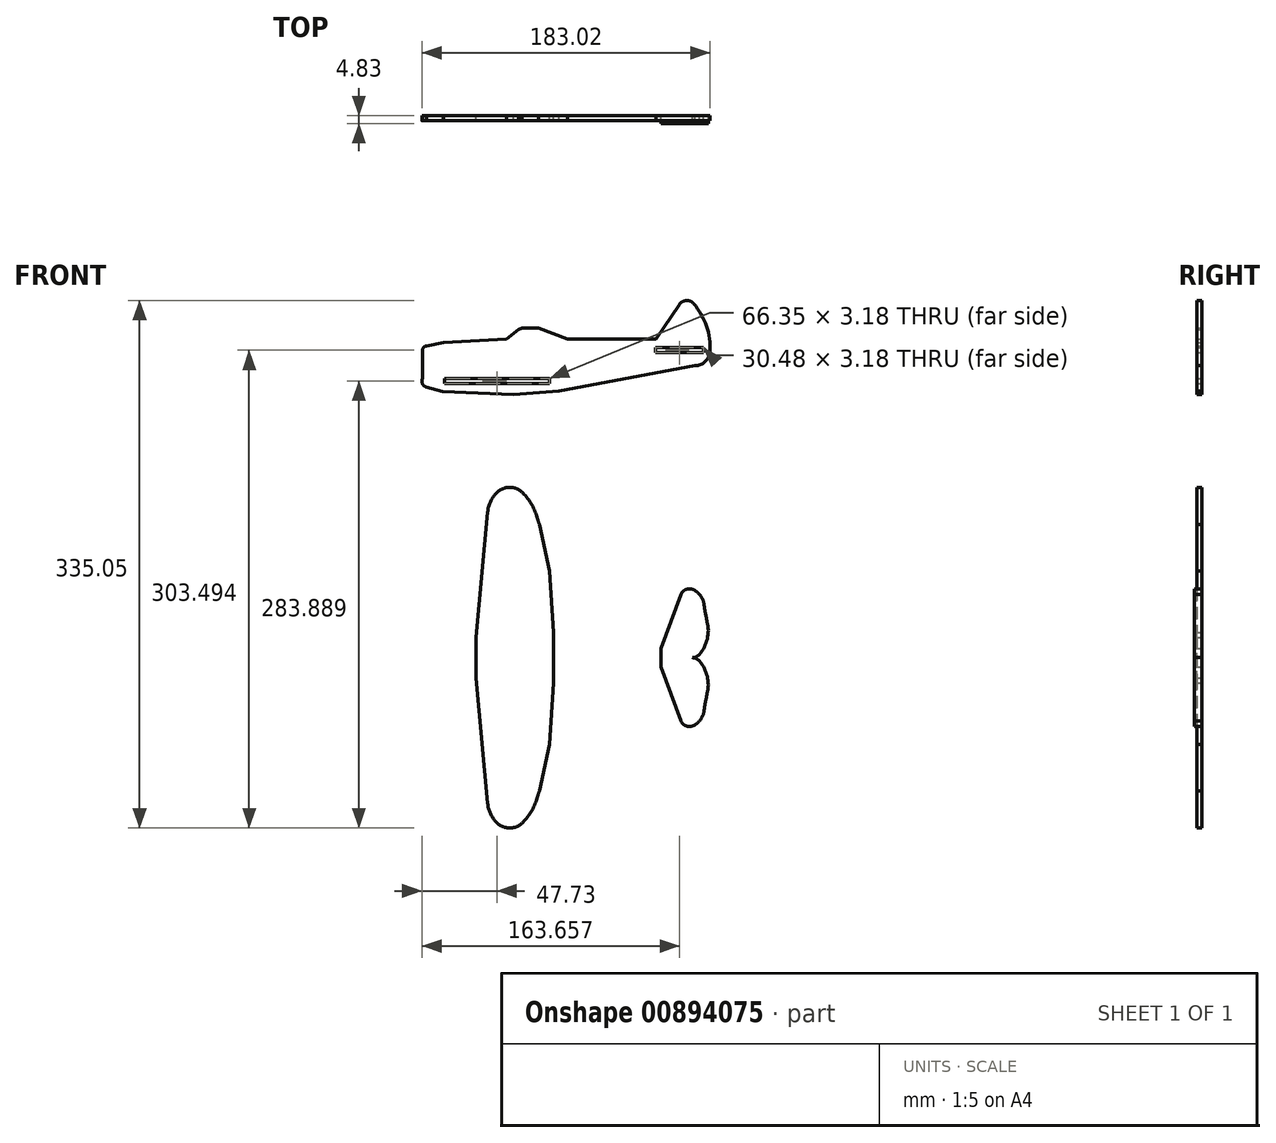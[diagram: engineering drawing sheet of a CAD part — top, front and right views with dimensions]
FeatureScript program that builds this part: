
annotation { "Feature Type Name" : "Feature", "Feature Type Description" : "" }
export const myFeature = defineFeature(function(context is Context, id is Id, definition is map)
    precondition{}
    {
        {
            var Q0;
            Q0=qCreatedBy(makeId("Front.planeOp"),FACE);
            var sketch = newSketch(context, id + "F0", { "sketchPlane" : qUnion([Q0])});
            skSolve(sketch);
        }
        {
            var Q0;
            Q0=qCreatedBy(makeId("Front.planeOp"),FACE);
            var sketch = newSketch(context, id + "F1", { "sketchPlane" : qUnion([Q0])});
            skLineSegment(sketch, "E0", {"start": v(-214.81, 114.42) * mm, "end": v(-29.22, 114.42) * mm, "construction": true});
            skLineSegment(sketch, "E1", {"start": v(-180, 114.42) * mm, "end": v(-180, 127.23) * mm, "construction": true});
            skLineSegment(sketch, "E2", {"start": v(-180, 127.23) * mm, "end": v(-172.61, 206.88) * mm});
            skArc(sketch, "E3", {"start": v(-172.61, 206.88) * mm, "mid": v(-170.85, 213.46) * mm, "end": v(-166.99, 219.08) * mm});
            skArc(sketch, "E4", {"start": v(-166.99, 219.08) * mm, "mid": v(-158.64, 222.6) * mm, "end": v(-150.3, 219.08) * mm});
            skArc(sketch, "E5", {"start": v(-150.3, 219.08) * mm, "mid": v(-144.52, 211.4) * mm, "end": v(-140.84, 202.54) * mm});
            skArc(sketch, "E6", {"start": v(-140.84, 202.54) * mm, "mid": v(-140.34, 200.83) * mm, "end": v(-139.8, 199.12) * mm});
            skLineSegment(sketch, "E7", {"start": v(-139.8, 199.12) * mm, "end": v(-133.44, 169.53) * mm});
            skLineSegment(sketch, "E8", {"start": v(-133.44, 169.53) * mm, "end": v(-130.81, 130.44) * mm});
            skLineSegment(sketch, "E9", {"start": v(-130.81, 130.44) * mm, "end": v(-130.81, 114.42) * mm});
            skLineSegment(sketch, "E10", {"start": v(-180, 114.42) * mm, "end": v(-180, 127.23) * mm});
            skLineSegment(sketch, "E11", {"start": v(-62.56, 114.42) * mm, "end": v(-62.56, 120.3) * mm});
            skLineSegment(sketch, "E12", {"start": v(-62.56, 120.3) * mm, "end": v(-49.89, 154.49) * mm});
            skArc(sketch, "E13", {"start": v(-49.89, 154.49) * mm, "mid": v(-48.63, 156.46) * mm, "end": v(-46.68, 157.74) * mm});
            skArc(sketch, "E14", {"start": v(-46.68, 157.74) * mm, "mid": v(-44.45, 158.15) * mm, "end": v(-42.23, 157.74) * mm});
            skArc(sketch, "E15", {"start": v(-42.23, 157.74) * mm, "mid": v(-39.9, 156.42) * mm, "end": v(-38.08, 154.49) * mm});
            skArc(sketch, "E16", {"start": v(-38.08, 154.49) * mm, "mid": v(-36.15, 151.58) * mm, "end": v(-35.18, 148.24) * mm});
            skArc(sketch, "E17", {"start": v(-35.18, 148.24) * mm, "mid": v(-34.3, 142.72) * mm, "end": v(-33.15, 137.26) * mm});
            skArc(sketch, "E18", {"start": v(-33.15, 137.26) * mm, "mid": v(-33.14, 126.34) * mm, "end": v(-38.08, 116.6) * mm});
            skArc(sketch, "E19", {"start": v(-38.08, 116.6) * mm, "mid": v(-40.03, 115.06) * mm, "end": v(-42.43, 114.42) * mm});
            skLineSegment(sketch, "E20", {"start": v(-213.84, 291.87) * mm, "end": v(-213.84, 309.93) * mm});
            skArc(sketch, "E21", {"start": v(-213.84, 309.93) * mm, "mid": v(-213.17, 311.66) * mm, "end": v(-211.52, 312.49) * mm});
            skLineSegment(sketch, "E22", {"start": v(-211.52, 312.49) * mm, "end": v(-200.55, 314.65) * mm});
            skLineSegment(sketch, "E23", {"start": v(-200.55, 314.65) * mm, "end": v(-160.75, 316.67) * mm});
            skLineSegment(sketch, "E24", {"start": v(-160.75, 316.67) * mm, "end": v(-152.96, 322.87) * mm});
            skLineSegment(sketch, "E25", {"start": v(-152.96, 322.87) * mm, "end": v(-150.65, 323.8) * mm});
            skLineSegment(sketch, "E26", {"start": v(-150.65, 323.8) * mm, "end": v(-140.2, 323.8) * mm});
            skLineSegment(sketch, "E27", {"start": v(-140.2, 323.8) * mm, "end": v(-121.96, 316.67) * mm});
            skLineSegment(sketch, "E28", {"start": v(-65.82, 316.67) * mm, "end": v(-50.84, 338.76) * mm});
            skArc(sketch, "E29", {"start": v(-50.84, 338.76) * mm, "mid": v(-46.41, 341.28) * mm, "end": v(-41.72, 339.29) * mm});
            skArc(sketch, "E30", {"start": v(-41.72, 339.29) * mm, "mid": v(-33.62, 325.05) * mm, "end": v(-31.44, 308.8) * mm});
            skArc(sketch, "E31", {"start": v(-31.44, 308.8) * mm, "mid": v(-34.41, 302.47) * mm, "end": v(-40.94, 299.95) * mm});
            skLineSegment(sketch, "E32", {"start": v(-40.94, 299.95) * mm, "end": v(-127.43, 283.8) * mm});
            skLineSegment(sketch, "E33", {"start": v(-127.43, 283.8) * mm, "end": v(-156.09, 281.71) * mm});
            skLineSegment(sketch, "E34", {"start": v(-156.09, 281.71) * mm, "end": v(-201.28, 283.4) * mm});
            skLineSegment(sketch, "E35", {"start": v(-201.28, 283.4) * mm, "end": v(-211.7, 286.4) * mm});
            skArc(sketch, "E36", {"start": v(-211.7, 286.4) * mm, "mid": v(-214.12, 288.6) * mm, "end": v(-213.84, 291.87) * mm});
            skArc(sketch, "E37.MirrorCS", {"start": v(-140.84, 26.3) * mm, "mid": v(-140.34, 28.02) * mm, "end": v(-139.8, 29.73) * mm});
            skLineSegment(sketch, "E38.MirrorCS", {"start": v(-180, 114.42) * mm, "end": v(-180, 101.62) * mm, "construction": true});
            skLineSegment(sketch, "E39.MirrorCS", {"start": v(-139.8, 29.73) * mm, "end": v(-133.44, 59.32) * mm});
            skArc(sketch, "E40.MirrorCS", {"start": v(-166.99, 9.77) * mm, "mid": v(-158.64, 6.24) * mm, "end": v(-150.3, 9.77) * mm});
            skArc(sketch, "E41.MirrorCS", {"start": v(-172.61, 21.97) * mm, "mid": v(-170.85, 15.39) * mm, "end": v(-166.99, 9.77) * mm});
            skLineSegment(sketch, "E42.MirrorCS", {"start": v(-133.44, 59.32) * mm, "end": v(-130.81, 98.4) * mm});
            skLineSegment(sketch, "E43.MirrorCS", {"start": v(-180, 114.42) * mm, "end": v(-180, 101.62) * mm});
            skLineSegment(sketch, "E44.MirrorCS", {"start": v(-180, 101.62) * mm, "end": v(-172.61, 21.97) * mm});
            skArc(sketch, "E45.MirrorCS", {"start": v(-150.3, 9.77) * mm, "mid": v(-144.52, 17.44) * mm, "end": v(-140.84, 26.3) * mm});
            skLineSegment(sketch, "E46.MirrorCS", {"start": v(-130.81, 98.4) * mm, "end": v(-130.81, 114.42) * mm});
            skArc(sketch, "E47.MirrorCS", {"start": v(-42.23, 71.11) * mm, "mid": v(-39.9, 72.43) * mm, "end": v(-38.08, 74.36) * mm});
            skArc(sketch, "E48.MirrorCS", {"start": v(-46.68, 71.11) * mm, "mid": v(-44.45, 70.7) * mm, "end": v(-42.23, 71.11) * mm});
            skArc(sketch, "E49.MirrorCS", {"start": v(-49.89, 74.36) * mm, "mid": v(-48.63, 72.4) * mm, "end": v(-46.68, 71.11) * mm});
            skArc(sketch, "E50.MirrorCS", {"start": v(-38.08, 112.26) * mm, "mid": v(-40.03, 113.8) * mm, "end": v(-42.43, 114.42) * mm});
            skLineSegment(sketch, "E51.MirrorCS", {"start": v(-62.56, 114.42) * mm, "end": v(-62.56, 108.55) * mm});
            skLineSegment(sketch, "E52.MirrorCS", {"start": v(-62.56, 108.55) * mm, "end": v(-49.89, 74.36) * mm});
            skArc(sketch, "E53.MirrorCS", {"start": v(-35.18, 80.61) * mm, "mid": v(-34.3, 86.13) * mm, "end": v(-33.15, 91.59) * mm});
            skArc(sketch, "E54.MirrorCS", {"start": v(-33.15, 91.59) * mm, "mid": v(-33.14, 102.51) * mm, "end": v(-38.08, 112.26) * mm});
            skArc(sketch, "E55.MirrorCS", {"start": v(-38.08, 74.36) * mm, "mid": v(-36.15, 77.27) * mm, "end": v(-35.18, 80.61) * mm});
            skLineSegment(sketch, "E56", {"start": v(-121.96, 316.67) * mm, "end": v(-65.82, 316.67) * mm});
            skSolve(sketch);
        }
        {
            var Q0;
            Q0=makeQuery(id+"F1.imprint","IMPRINT",FACE,{"disambiguationData":[TD([[makeQuery(id+"F1.imprint","IMPRINT",EDGE,{"derivedFrom":sQuery(id+"F1.wireOp",EDGE,"E2")}),-1.0]])]});
            var Q1;
            Q1=makeQuery(id+"F1.imprint","IMPRINT",FACE,{"disambiguationData":[TD([[makeQuery(id+"F1.imprint","IMPRINT",EDGE,{"derivedFrom":sQuery(id+"F1.wireOp",EDGE,"E20")}),-1.0]])]});
            var Q2;
            Q2=makeQuery(id+"F1.imprint","IMPRINT",FACE,{"disambiguationData":[TD([[makeQuery(id+"F1.imprint","IMPRINT",EDGE,{"derivedFrom":sQuery(id+"F1.wireOp",EDGE,"E11")}),-1.0]])]});
            extrude(context, id + "F2", {"entities" : qUnion([Q0, Q1, Q2]), "depth" : 3.17 * mm, "offsetDistance" : 25.4 * mm});
        }
        {
            var Q0;
            Q0=makeQuery(id+"F2.opExtrude","CAP_FACE",FACE,{"disambiguationData":[OSD([sQuery(id+"F1.wireOp",EDGE,"E20"),sQuery(id+"F1.wireOp",EDGE,"E21"),sQuery(id+"F1.wireOp",EDGE,"E22"),sQuery(id+"F1.wireOp",EDGE,"E23"),sQuery(id+"F1.wireOp",EDGE,"E24"),sQuery(id+"F1.wireOp",EDGE,"E25"),sQuery(id+"F1.wireOp",EDGE,"E26"),sQuery(id+"F1.wireOp",EDGE,"E27"),sQuery(id+"F1.wireOp",EDGE,"E28"),sQuery(id+"F1.wireOp",EDGE,"E29"),sQuery(id+"F1.wireOp",EDGE,"E30"),sQuery(id+"F1.wireOp",EDGE,"E31"),sQuery(id+"F1.wireOp",EDGE,"E32"),sQuery(id+"F1.wireOp",EDGE,"E33"),sQuery(id+"F1.wireOp",EDGE,"E34"),sQuery(id+"F1.wireOp",EDGE,"E35"),sQuery(id+"F1.wireOp",EDGE,"E36"),sQuery(id+"F1.wireOp",EDGE,"E56")])],"isStart":false});
            extrude(context, id + "F3", {"entities" : qUnion([Q0]), "operationType" : NewBodyOperationType.ADD, "depth" : 1 / 203.2 * mm, "offsetDistance" : 25.4 * mm});
        }
        {
            var Q0;
            Q0=qCreatedBy(makeId("Front.planeOp"),FACE);
            var sketch = newSketch(context, id + "F4", { "sketchPlane" : qUnion([Q0])});
            skLineSegment(sketch, "E57.bottom", {"start": v(-199.83, 291.72) * mm, "end": v(-133.47, 291.72) * mm});
            skLineSegment(sketch, "E57.top", {"start": v(-199.83, 288.54) * mm, "end": v(-133.47, 288.54) * mm});
            skLineSegment(sketch, "E57.left", {"start": v(-199.83, 291.72) * mm, "end": v(-199.83, 288.54) * mm});
            skLineSegment(sketch, "E57.right", {"start": v(-133.47, 291.72) * mm, "end": v(-133.47, 288.54) * mm});
            skLineSegment(sketch, "E58.bottom", {"start": v(-65.96, 311.32) * mm, "end": v(-35.48, 311.32) * mm});
            skLineSegment(sketch, "E58.top", {"start": v(-65.96, 308.15) * mm, "end": v(-35.48, 308.15) * mm});
            skLineSegment(sketch, "E58.left", {"start": v(-65.96, 311.32) * mm, "end": v(-65.96, 308.15) * mm});
            skLineSegment(sketch, "E58.right", {"start": v(-35.48, 311.32) * mm, "end": v(-35.48, 308.15) * mm});
            skLineSegment(sketch, "E59", {"start": v(-180.49, 127.2) * mm, "end": v(-180.49, 99.94) * mm, "construction": true});
            skLineSegment(sketch, "E60", {"start": v(-62.89, 115.5) * mm, "end": v(-35.32, 115.5) * mm, "construction": true});
            skSolve(sketch);
        }
        {
            var Q0;
            Q0 = qSketchRegion(id + "F4", true);
            extrude(context, id + "F5", {"entities" : qUnion([Q0]), "operationType" : NewBodyOperationType.REMOVE, "endBound" : BoundingType.THROUGH_ALL, "depth" : 25.4 * mm, "offsetDistance" : 25.4 * mm});
        }
        {
            var Q0;
            Q0 = qSketchRegion(id + "F0", true);
            var Q1;
            Q1=makeQuery(id+"F2.opExtrude","CAP_FACE",FACE,{"disambiguationData":[OSD([sQuery(id+"F1.wireOp",EDGE,"E11"),sQuery(id+"F1.wireOp",EDGE,"E12"),sQuery(id+"F1.wireOp",EDGE,"E13"),sQuery(id+"F1.wireOp",EDGE,"E14"),sQuery(id+"F1.wireOp",EDGE,"E15"),sQuery(id+"F1.wireOp",EDGE,"E16"),sQuery(id+"F1.wireOp",EDGE,"E17"),sQuery(id+"F1.wireOp",EDGE,"E18"),sQuery(id+"F1.wireOp",EDGE,"E19"),sQuery(id+"F1.wireOp",EDGE,"E47.MirrorCS"),sQuery(id+"F1.wireOp",EDGE,"E48.MirrorCS"),sQuery(id+"F1.wireOp",EDGE,"E49.MirrorCS"),sQuery(id+"F1.wireOp",EDGE,"E50.MirrorCS"),sQuery(id+"F1.wireOp",EDGE,"E51.MirrorCS"),sQuery(id+"F1.wireOp",EDGE,"E52.MirrorCS"),sQuery(id+"F1.wireOp",EDGE,"E53.MirrorCS"),sQuery(id+"F1.wireOp",EDGE,"E54.MirrorCS"),sQuery(id+"F1.wireOp",EDGE,"E55.MirrorCS")])],"isStart":false});
            extrude(context, id + "F6", {"entities" : qUnion([Q0, Q1]), "operationType" : NewBodyOperationType.ADD, "depth" : 1.65 * mm, "offsetDistance" : 25.4 * mm});
        }
    });
